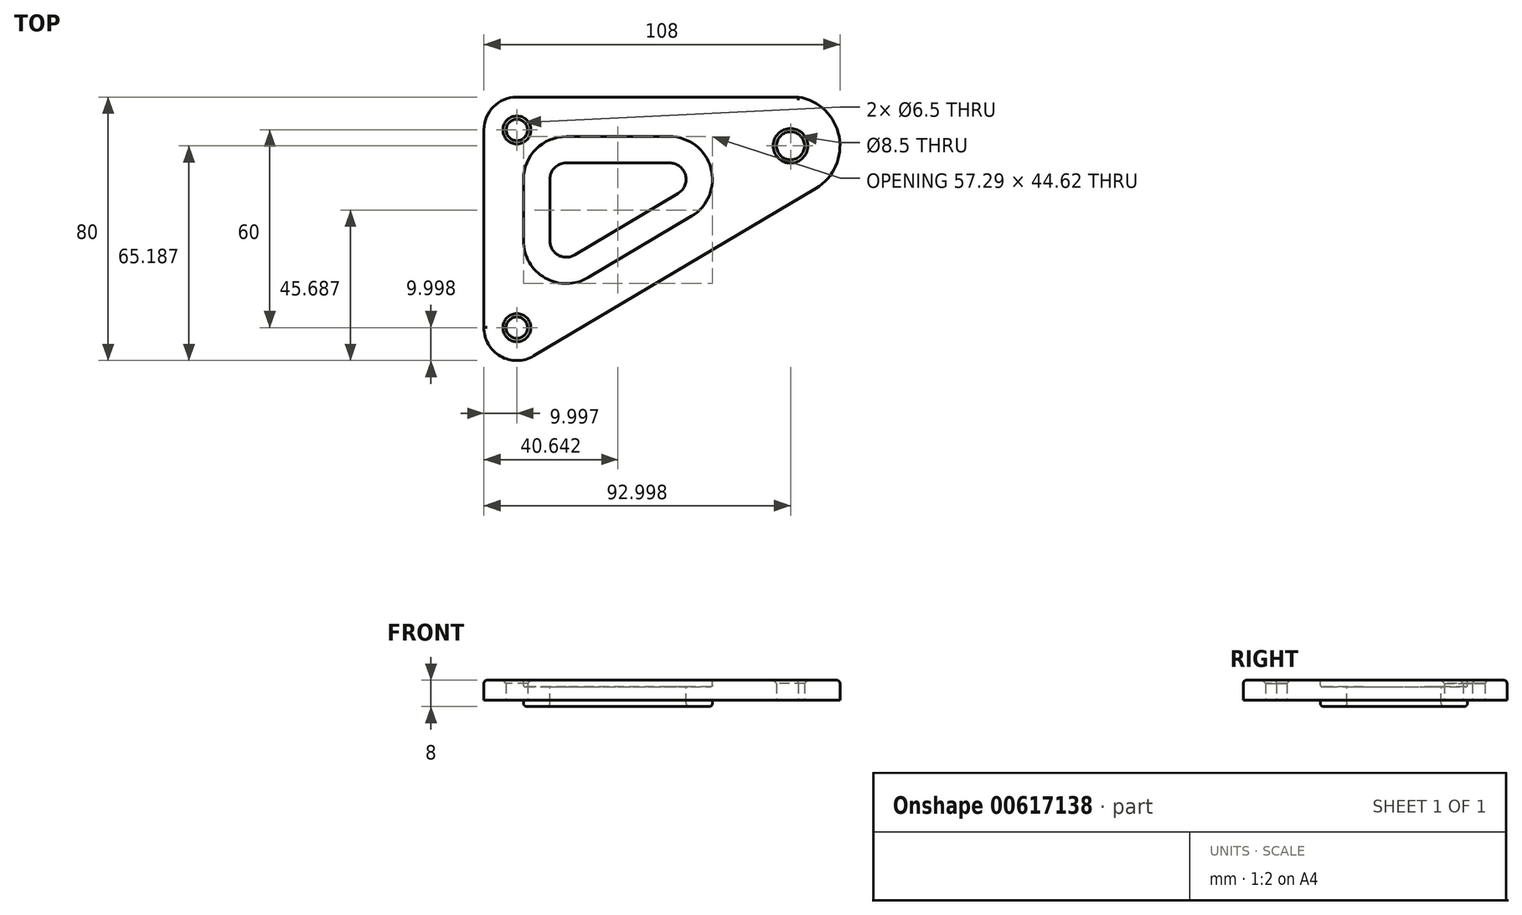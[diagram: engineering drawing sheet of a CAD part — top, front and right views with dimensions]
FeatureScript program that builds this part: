
annotation { "Feature Type Name" : "Feature", "Feature Type Description" : "" }
export const myFeature = defineFeature(function(context is Context, id is Id, definition is map)
    precondition{}
    {
        {
            var Q0;
            Q0=qCreatedBy(makeId("Top.planeOp"),FACE);
            var sketch = newSketch(context, id + "F0", { "sketchPlane" : qUnion([Q0])});
            skCircle(sketch, "E0", {"center": v(-62.86, 16.69) * mm, "radius": 3.25 * mm});
            skCircle(sketch, "E1", {"center": v(-62.86, -43.31) * mm, "radius": 3.25 * mm});
            skCircle(sketch, "E2", {"center": v(20.14, 11.88) * mm, "radius": 4.25 * mm});
            skArc(sketch, "E3", {"start": v(-62.86, 26.69) * mm, "mid": v(-69.93, 23.76) * mm, "end": v(-72.86, 16.69) * mm});
            skArc(sketch, "E4", {"start": v(-72.86, -43.2) * mm, "mid": v(-67.86, -51.98) * mm, "end": v(-57.75, -51.9) * mm});
            skArc(sketch, "E5", {"start": v(27.8, -1.01) * mm, "mid": v(34.24, 16.99) * mm, "end": v(17.76, 26.69) * mm});
            skLineSegment(sketch, "E6", {"start": v(-72.86, -43.2) * mm, "end": v(-72.86, 16.69) * mm});
            skLineSegment(sketch, "E7", {"start": v(-57.75, -51.9) * mm, "end": v(29.51, 0) * mm});
            skLineSegment(sketch, "E8", {"start": v(22.51, 26.69) * mm, "end": v(-62.86, 26.69) * mm});
            skSolve(sketch);
        }
        {
            var Q0;
            Q0=makeQuery(id+"F0.imprint","IMPRINT",FACE,{"disambiguationData":[TD([[makeQuery(id+"F0.imprint","IMPRINT",EDGE,{"derivedFrom":sQuery(id+"F0.wireOp",EDGE,"E0")}),-1.0]])]});
            extrude(context, id + "F1", {"entities" : qUnion([Q0]), "depth" : 8 * mm, "offsetDistance" : 25 * mm});
        }
        {
            var Q0;
            Q0=makeQuery(id+"F1.opExtrude","CAP_FACE",FACE,{"disambiguationData":[OSD([sQuery(id+"F0.wireOp",EDGE,"E0"),sQuery(id+"F0.wireOp",EDGE,"E1"),sQuery(id+"F0.wireOp",EDGE,"E2"),sQuery(id+"F0.wireOp",EDGE,"E3"),sQuery(id+"F0.wireOp",EDGE,"E4"),sQuery(id+"F0.wireOp",EDGE,"E5"),sQuery(id+"F0.wireOp",EDGE,"E6"),sQuery(id+"F0.wireOp",EDGE,"E7"),sQuery(id+"F0.wireOp",EDGE,"E8")])],"isStart":false});
            var sketch = newSketch(context, id + "F2", { "sketchPlane" : qUnion([Q0])});
            skLineSegment(sketch, "E9.0", {"start": v(-16.55, 6.69) * mm, "end": v(-47.86, 6.69) * mm});
            skLineSegment(sketch, "E9.1", {"start": v(-45.3, -21.23) * mm, "end": v(-14, -2.6) * mm});
            skLineSegment(sketch, "E9.2", {"start": v(-52.86, -16.94) * mm, "end": v(-52.86, 1.69) * mm});
            skPoint(sketch, "E10.visualSharp", {"position": v(-52.86, 6.69) * mm});
            skArc(sketch, "E10.filletArc", {"start": v(-47.86, 6.69) * mm, "mid": v(-51.4, 5.22) * mm, "end": v(-52.86, 1.69) * mm});
            skPoint(sketch, "E11.visualSharp", {"position": v(-52.86, -25.73) * mm});
            skArc(sketch, "E11.filletArc", {"start": v(-52.86, -16.94) * mm, "mid": v(-50.33, -21.28) * mm, "end": v(-45.3, -21.23) * mm});
            skPoint(sketch, "E12.visualSharp", {"position": v(1.63, 6.69) * mm});
            skArc(sketch, "E12.filletArc", {"start": v(-14, -2.6) * mm, "mid": v(-11.73, 3.01) * mm, "end": v(-16.55, 6.69) * mm});
            skSolve(sketch);
        }
        {
            var Q0;
            Q0=makeQuery(id+"F2.imprint","IMPRINT",FACE,{"disambiguationData":[TD([[makeQuery(id+"F2.imprint","IMPRINT",EDGE,{"derivedFrom":sQuery(id+"F2.wireOp",EDGE,"E9.0")}),1.0]])]});
            extrude(context, id + "F3", {"entities" : qUnion([Q0]), "operationType" : NewBodyOperationType.REMOVE, "oppositeDirection" : true, "depth" : 25 * mm, "offsetDistance" : 25 * mm});
        }
        {
            var Q0;
            Q0=makeQuery(id+"F1.opExtrude","CAP_FACE",FACE,{"disambiguationData":[OSD([sQuery(id+"F0.wireOp",EDGE,"E0"),sQuery(id+"F0.wireOp",EDGE,"E1"),sQuery(id+"F0.wireOp",EDGE,"E2"),sQuery(id+"F0.wireOp",EDGE,"E3"),sQuery(id+"F0.wireOp",EDGE,"E4"),sQuery(id+"F0.wireOp",EDGE,"E5"),sQuery(id+"F0.wireOp",EDGE,"E6"),sQuery(id+"F0.wireOp",EDGE,"E7"),sQuery(id+"F0.wireOp",EDGE,"E8")])],"isStart":false});
            var sketch = newSketch(context, id + "F4", { "sketchPlane" : qUnion([Q0])});
            skArc(sketch, "E13.0", {"start": v(-60.86, -16.94) * mm, "mid": v(-54.29, -28.24) * mm, "end": v(-41.22, -28.1) * mm});
            skArc(sketch, "E13.1", {"start": v(-47.86, 14.69) * mm, "mid": v(-57.05, 10.88) * mm, "end": v(-60.86, 1.69) * mm});
            skLineSegment(sketch, "E13.2", {"start": v(-16.55, 14.69) * mm, "end": v(-47.86, 14.69) * mm});
            skLineSegment(sketch, "E13.3", {"start": v(-60.86, -16.94) * mm, "end": v(-60.86, 1.69) * mm});
            skArc(sketch, "E13.4", {"start": v(-9.9, -9.48) * mm, "mid": v(-4.02, 5.13) * mm, "end": v(-16.55, 14.69) * mm});
            skLineSegment(sketch, "E13.5", {"start": v(-41.22, -28.1) * mm, "end": v(-9.9, -9.48) * mm});
            skArc(sketch, "E14.0", {"start": v(-77.86, -43.17) * mm, "mid": v(-70.34, -56.32) * mm, "end": v(-55.2, -56.2) * mm});
            skArc(sketch, "E14.1", {"start": v(30.36, -5.31) * mm, "mid": v(39.74, 15.84) * mm, "end": v(22.88, 31.69) * mm});
            skLineSegment(sketch, "E14.2", {"start": v(22.88, 31.69) * mm, "end": v(-62.86, 31.69) * mm});
            skLineSegment(sketch, "E14.3", {"start": v(-55.2, -56.2) * mm, "end": v(30.36, -5.31) * mm});
            skArc(sketch, "E14.4", {"start": v(-62.86, 31.69) * mm, "mid": v(-73.47, 27.3) * mm, "end": v(-77.86, 16.69) * mm});
            skLineSegment(sketch, "E14.5", {"start": v(-77.86, 16.69) * mm, "end": v(-77.86, -43.17) * mm});
            skSolve(sketch);
        }
        {
            var Q0;
            Q0=makeQuery(id+"F4.imprint","IMPRINT",FACE,{"disambiguationData":[TD([[makeQuery(id+"F4.imprint","IMPRINT",EDGE,{"derivedFrom":sQuery(id+"F4.wireOp",EDGE,"E13.0")}),1.0]])]});
            extrude(context, id + "F5", {"entities" : qUnion([Q0]), "operationType" : NewBodyOperationType.REMOVE, "oppositeDirection" : true, "depth" : 2 * mm, "offsetDistance" : 25 * mm});
        }
        {
            var Q0;
            Q0=makeQuery(id+"F1.opExtrude","CAP_FACE",FACE,{"disambiguationData":[OSD([sQuery(id+"F0.wireOp",EDGE,"E0"),sQuery(id+"F0.wireOp",EDGE,"E1"),sQuery(id+"F0.wireOp",EDGE,"E2"),sQuery(id+"F0.wireOp",EDGE,"E3"),sQuery(id+"F0.wireOp",EDGE,"E4"),sQuery(id+"F0.wireOp",EDGE,"E5"),sQuery(id+"F0.wireOp",EDGE,"E6"),sQuery(id+"F0.wireOp",EDGE,"E7"),sQuery(id+"F0.wireOp",EDGE,"E8")])],"isStart":true});
            var sketch = newSketch(context, id + "F6", { "sketchPlane" : qUnion([Q0])});
            skArc(sketch, "E15.0", {"start": v(-9.9, 9.48) * mm, "mid": v(-4.02, -5.13) * mm, "end": v(-16.55, -14.69) * mm});
            skArc(sketch, "E15.1", {"start": v(-47.86, -14.69) * mm, "mid": v(-57.05, -10.88) * mm, "end": v(-60.86, -1.69) * mm});
            skLineSegment(sketch, "E15.2", {"start": v(-60.86, 16.94) * mm, "end": v(-60.86, -1.69) * mm});
            skLineSegment(sketch, "E15.3", {"start": v(-16.55, -14.69) * mm, "end": v(-47.86, -14.69) * mm});
            skArc(sketch, "E15.4", {"start": v(-60.86, 16.94) * mm, "mid": v(-54.29, 28.24) * mm, "end": v(-41.22, 28.1) * mm});
            skLineSegment(sketch, "E15.5", {"start": v(-41.22, 28.1) * mm, "end": v(-9.9, 9.48) * mm});
            skSolve(sketch);
        }
        {
            var Q0;
            Q0=makeQuery(id+"F6.imprint","IMPRINT",FACE,{"disambiguationData":[TD([[makeQuery(id+"F6.imprint","IMPRINT",EDGE,{"derivedFrom":sQuery(id+"F6.wireOp",EDGE,"E15.0")}),-1.0]])]});
            extrude(context, id + "F7", {"entities" : qUnion([Q0]), "operationType" : NewBodyOperationType.REMOVE, "oppositeDirection" : true, "depth" : 2 * mm, "offsetDistance" : 25 * mm});
        }
        {
            var Q0;
            Q0=makeQuery(id+"F5.boolean.opBoolean","COPY",EDGE,{"derivedFrom":makeQuery(id+"F5.opExtrude","CAP_EDGE",EDGE,{"disambiguationData":[OSD([sQuery(id+"F4.wireOp",EDGE,"E13.1")])],"isStart":true})});
            var Q1;
            Q1=makeQuery(id+"F5.boolean.opBoolean","COPY",EDGE,{"derivedFrom":makeQuery(id+"F5.opExtrude","CAP_EDGE",EDGE,{"disambiguationData":[OSD([sQuery(id+"F4.wireOp",EDGE,"E13.2")])],"isStart":true})});
            var Q2;
            Q2=makeQuery(id+"F5.boolean.opBoolean","COPY",EDGE,{"derivedFrom":makeQuery(id+"F5.opExtrude","CAP_EDGE",EDGE,{"disambiguationData":[OSD([sQuery(id+"F4.wireOp",EDGE,"E13.4")])],"isStart":true})});
            var Q3;
            Q3=makeQuery(id+"F5.boolean.opBoolean","COPY",EDGE,{"derivedFrom":makeQuery(id+"F5.opExtrude","CAP_EDGE",EDGE,{"disambiguationData":[OSD([sQuery(id+"F4.wireOp",EDGE,"E13.5")])],"isStart":true})});
            var Q4;
            Q4=makeQuery(id+"F5.boolean.opBoolean","COPY",EDGE,{"derivedFrom":makeQuery(id+"F5.opExtrude","CAP_EDGE",EDGE,{"disambiguationData":[OSD([sQuery(id+"F4.wireOp",EDGE,"E13.0")])],"isStart":true})});
            var Q5;
            Q5=makeQuery(id+"F5.boolean.opBoolean","COPY",EDGE,{"derivedFrom":makeQuery(id+"F5.opExtrude","CAP_EDGE",EDGE,{"disambiguationData":[OSD([sQuery(id+"F4.wireOp",EDGE,"E13.3")])],"isStart":true})});
            var Q6;
            Q6=makeQuery(id+"F5.boolean.opBoolean","COPY",EDGE,{"derivedFrom":makeQuery(id+"F5.opExtrude","CAP_EDGE",EDGE,{"disambiguationData":[OSD([sQuery(id+"F2.wireOp",EDGE,"E9.2")])],"isStart":false})});
            var Q7;
            Q7=makeQuery(id+"F5.boolean.opBoolean","COPY",EDGE,{"derivedFrom":makeQuery(id+"F5.opExtrude","CAP_EDGE",EDGE,{"disambiguationData":[OSD([sQuery(id+"F2.wireOp",EDGE,"E10.filletArc")])],"isStart":false})});
            var Q8;
            Q8=makeQuery(id+"F5.boolean.opBoolean","COPY",EDGE,{"derivedFrom":makeQuery(id+"F5.opExtrude","CAP_EDGE",EDGE,{"disambiguationData":[OSD([sQuery(id+"F2.wireOp",EDGE,"E9.0")])],"isStart":false})});
            var Q9;
            Q9=makeQuery(id+"F5.boolean.opBoolean","COPY",FACE,{"derivedFrom":makeQuery(id+"F5.opExtrude","CAP_FACE",FACE,{"disambiguationData":[OSD([sQuery(id+"F2.wireOp",EDGE,"E9.0"),sQuery(id+"F2.wireOp",EDGE,"E9.1"),sQuery(id+"F2.wireOp",EDGE,"E9.2"),sQuery(id+"F2.wireOp",EDGE,"E10.filletArc"),sQuery(id+"F2.wireOp",EDGE,"E11.filletArc"),sQuery(id+"F2.wireOp",EDGE,"E12.filletArc"),sQuery(id+"F4.wireOp",EDGE,"E13.0"),sQuery(id+"F4.wireOp",EDGE,"E13.1"),sQuery(id+"F4.wireOp",EDGE,"E13.2"),sQuery(id+"F4.wireOp",EDGE,"E13.3"),sQuery(id+"F4.wireOp",EDGE,"E13.4"),sQuery(id+"F4.wireOp",EDGE,"E13.5")])],"isStart":false})});
            var Q10;
            Q10=makeQuery(id+"F7.boolean.opBoolean","COPY",EDGE,{"derivedFrom":makeQuery(id+"F7.opExtrude","CAP_EDGE",EDGE,{"disambiguationData":[OSD([sQuery(id+"F6.wireOp",EDGE,"E15.2")])],"isStart":true})});
            var Q11;
            Q11=makeQuery(id+"F7.boolean.opBoolean","COPY",EDGE,{"derivedFrom":makeQuery(id+"F7.opExtrude","CAP_EDGE",EDGE,{"disambiguationData":[OSD([sQuery(id+"F6.wireOp",EDGE,"E15.4")])],"isStart":true})});
            var Q12;
            Q12=makeQuery(id+"F7.boolean.opBoolean","COPY",EDGE,{"derivedFrom":makeQuery(id+"F7.opExtrude","CAP_EDGE",EDGE,{"disambiguationData":[OSD([sQuery(id+"F6.wireOp",EDGE,"E15.5")])],"isStart":true})});
            var Q13;
            Q13=makeQuery(id+"F7.boolean.opBoolean","COPY",EDGE,{"derivedFrom":makeQuery(id+"F7.opExtrude","CAP_EDGE",EDGE,{"disambiguationData":[OSD([sQuery(id+"F6.wireOp",EDGE,"E15.0")])],"isStart":true})});
            var Q14;
            Q14=makeQuery(id+"F7.boolean.opBoolean","COPY",EDGE,{"derivedFrom":makeQuery(id+"F7.opExtrude","CAP_EDGE",EDGE,{"disambiguationData":[OSD([sQuery(id+"F6.wireOp",EDGE,"E15.3")])],"isStart":true})});
            var Q15;
            Q15=makeQuery(id+"F7.boolean.opBoolean","COPY",EDGE,{"derivedFrom":makeQuery(id+"F7.opExtrude","CAP_EDGE",EDGE,{"disambiguationData":[OSD([sQuery(id+"F6.wireOp",EDGE,"E15.1")])],"isStart":true})});
            var Q16;
            Q16=makeQuery(id+"F7.boolean.opBoolean","COPY",EDGE,{"derivedFrom":makeQuery(id+"F7.opExtrude","CAP_EDGE",EDGE,{"disambiguationData":[OSD([sQuery(id+"F0.wireOp",EDGE,"E0"),sQuery(id+"F0.wireOp",EDGE,"E1"),sQuery(id+"F0.wireOp",EDGE,"E2"),sQuery(id+"F0.wireOp",EDGE,"E3"),sQuery(id+"F0.wireOp",EDGE,"E4"),sQuery(id+"F0.wireOp",EDGE,"E5"),sQuery(id+"F0.wireOp",EDGE,"E6"),sQuery(id+"F0.wireOp",EDGE,"E7"),sQuery(id+"F0.wireOp",EDGE,"E8"),sQuery(id+"F2.wireOp",EDGE,"E9.0")])],"isStart":false})});
            var Q17;
            Q17=makeQuery(id+"F7.boolean.opBoolean","COPY",EDGE,{"derivedFrom":makeQuery(id+"F7.opExtrude","CAP_EDGE",EDGE,{"disambiguationData":[OSD([sQuery(id+"F0.wireOp",EDGE,"E0"),sQuery(id+"F0.wireOp",EDGE,"E1"),sQuery(id+"F0.wireOp",EDGE,"E2"),sQuery(id+"F0.wireOp",EDGE,"E3"),sQuery(id+"F0.wireOp",EDGE,"E4"),sQuery(id+"F0.wireOp",EDGE,"E5"),sQuery(id+"F0.wireOp",EDGE,"E6"),sQuery(id+"F0.wireOp",EDGE,"E7"),sQuery(id+"F0.wireOp",EDGE,"E8"),sQuery(id+"F2.wireOp",EDGE,"E10.filletArc")])],"isStart":false})});
            var Q18;
            Q18=makeQuery(id+"F7.boolean.opBoolean","COPY",EDGE,{"derivedFrom":makeQuery(id+"F7.opExtrude","CAP_EDGE",EDGE,{"disambiguationData":[OSD([sQuery(id+"F0.wireOp",EDGE,"E0"),sQuery(id+"F0.wireOp",EDGE,"E1"),sQuery(id+"F0.wireOp",EDGE,"E2"),sQuery(id+"F0.wireOp",EDGE,"E3"),sQuery(id+"F0.wireOp",EDGE,"E4"),sQuery(id+"F0.wireOp",EDGE,"E5"),sQuery(id+"F0.wireOp",EDGE,"E6"),sQuery(id+"F0.wireOp",EDGE,"E7"),sQuery(id+"F0.wireOp",EDGE,"E8"),sQuery(id+"F2.wireOp",EDGE,"E9.2")])],"isStart":false})});
            var Q19;
            Q19=makeQuery(id+"F7.boolean.opBoolean","COPY",EDGE,{"derivedFrom":makeQuery(id+"F7.opExtrude","CAP_EDGE",EDGE,{"disambiguationData":[OSD([sQuery(id+"F0.wireOp",EDGE,"E0"),sQuery(id+"F0.wireOp",EDGE,"E1"),sQuery(id+"F0.wireOp",EDGE,"E2"),sQuery(id+"F0.wireOp",EDGE,"E3"),sQuery(id+"F0.wireOp",EDGE,"E4"),sQuery(id+"F0.wireOp",EDGE,"E5"),sQuery(id+"F0.wireOp",EDGE,"E6"),sQuery(id+"F0.wireOp",EDGE,"E7"),sQuery(id+"F0.wireOp",EDGE,"E8"),sQuery(id+"F2.wireOp",EDGE,"E11.filletArc")])],"isStart":false})});
            var Q20;
            Q20=makeQuery(id+"F7.boolean.opBoolean","COPY",EDGE,{"derivedFrom":makeQuery(id+"F7.opExtrude","CAP_EDGE",EDGE,{"disambiguationData":[OSD([sQuery(id+"F0.wireOp",EDGE,"E0"),sQuery(id+"F0.wireOp",EDGE,"E1"),sQuery(id+"F0.wireOp",EDGE,"E2"),sQuery(id+"F0.wireOp",EDGE,"E3"),sQuery(id+"F0.wireOp",EDGE,"E4"),sQuery(id+"F0.wireOp",EDGE,"E5"),sQuery(id+"F0.wireOp",EDGE,"E6"),sQuery(id+"F0.wireOp",EDGE,"E7"),sQuery(id+"F0.wireOp",EDGE,"E8"),sQuery(id+"F2.wireOp",EDGE,"E9.1")])],"isStart":false})});
            var Q21;
            Q21=makeQuery(id+"F7.boolean.opBoolean","COPY",EDGE,{"derivedFrom":makeQuery(id+"F7.opExtrude","CAP_EDGE",EDGE,{"disambiguationData":[OSD([sQuery(id+"F0.wireOp",EDGE,"E0"),sQuery(id+"F0.wireOp",EDGE,"E1"),sQuery(id+"F0.wireOp",EDGE,"E2"),sQuery(id+"F0.wireOp",EDGE,"E3"),sQuery(id+"F0.wireOp",EDGE,"E4"),sQuery(id+"F0.wireOp",EDGE,"E5"),sQuery(id+"F0.wireOp",EDGE,"E6"),sQuery(id+"F0.wireOp",EDGE,"E7"),sQuery(id+"F0.wireOp",EDGE,"E8"),sQuery(id+"F2.wireOp",EDGE,"E12.filletArc")])],"isStart":false})});
            fillet(context, id + "F8", {"entities" : qUnion([Q0, Q1, Q2, Q3, Q4, Q5, Q6, Q7, Q8, Q9, Q10, Q11, Q12, Q13, Q14, Q15, Q16, Q17, Q18, Q19, Q20, Q21]), "radius" : 0.5 * mm, "tangentPropagation" : true, "allowEdgeOverflow" : false});
        }
        {
            var Q0;
            Q0=makeQuery(id+"F1.opExtrude","CAP_EDGE",EDGE,{"disambiguationData":[OSD([sQuery(id+"F0.wireOp",EDGE,"E3")])],"isStart":true});
            var Q1;
            Q1=makeQuery(id+"F1.opExtrude","CAP_EDGE",EDGE,{"disambiguationData":[OSD([sQuery(id+"F0.wireOp",EDGE,"E6")])],"isStart":true});
            var Q2;
            Q2=makeQuery(id+"F1.opExtrude","CAP_EDGE",EDGE,{"disambiguationData":[OSD([sQuery(id+"F0.wireOp",EDGE,"E4")])],"isStart":true});
            var Q3;
            Q3=makeQuery(id+"F1.opExtrude","CAP_EDGE",EDGE,{"disambiguationData":[OSD([sQuery(id+"F0.wireOp",EDGE,"E7")])],"isStart":true});
            var Q4;
            Q4=makeQuery(id+"F1.opExtrude","CAP_EDGE",EDGE,{"disambiguationData":[OSD([sQuery(id+"F0.wireOp",EDGE,"E5")])],"isStart":true});
            var Q5;
            Q5=makeQuery(id+"F1.opExtrude","CAP_FACE",FACE,{"disambiguationData":[OSD([sQuery(id+"F0.wireOp",EDGE,"E0"),sQuery(id+"F0.wireOp",EDGE,"E1"),sQuery(id+"F0.wireOp",EDGE,"E2"),sQuery(id+"F0.wireOp",EDGE,"E3"),sQuery(id+"F0.wireOp",EDGE,"E4"),sQuery(id+"F0.wireOp",EDGE,"E5"),sQuery(id+"F0.wireOp",EDGE,"E6"),sQuery(id+"F0.wireOp",EDGE,"E7"),sQuery(id+"F0.wireOp",EDGE,"E8")])],"isStart":true});
            var Q6;
            Q6=makeQuery(id+"F1.opExtrude","CAP_EDGE",EDGE,{"disambiguationData":[OSD([sQuery(id+"F0.wireOp",EDGE,"E5")])],"isStart":false});
            var Q7;
            Q7=makeQuery(id+"F1.opExtrude","CAP_EDGE",EDGE,{"disambiguationData":[OSD([sQuery(id+"F0.wireOp",EDGE,"E7")])],"isStart":false});
            var Q8;
            Q8=makeQuery(id+"F1.opExtrude","CAP_EDGE",EDGE,{"disambiguationData":[OSD([sQuery(id+"F0.wireOp",EDGE,"E4")])],"isStart":false});
            var Q9;
            Q9=makeQuery(id+"F1.opExtrude","CAP_EDGE",EDGE,{"disambiguationData":[OSD([sQuery(id+"F0.wireOp",EDGE,"E6")])],"isStart":false});
            var Q10;
            Q10=makeQuery(id+"F1.opExtrude","CAP_EDGE",EDGE,{"disambiguationData":[OSD([sQuery(id+"F0.wireOp",EDGE,"E3")])],"isStart":false});
            var Q11;
            Q11=makeQuery(id+"F1.opExtrude","CAP_EDGE",EDGE,{"disambiguationData":[OSD([sQuery(id+"F0.wireOp",EDGE,"E8")])],"isStart":false});
            fillet(context, id + "F9", {"entities" : qUnion([Q0, Q1, Q2, Q3, Q4, Q5, Q6, Q7, Q8, Q9, Q10, Q11]), "radius" : 1 * mm, "tangentPropagation" : true, "allowEdgeOverflow" : false});
        }
        {
            var Q0;
            Q0=makeQuery(id+"F1.opExtrude","CAP_EDGE",EDGE,{"disambiguationData":[OSD([sQuery(id+"F0.wireOp",EDGE,"E2")])],"isStart":false});
            var Q1;
            Q1=makeQuery(id+"F1.opExtrude","CAP_EDGE",EDGE,{"disambiguationData":[OSD([sQuery(id+"F0.wireOp",EDGE,"E1")])],"isStart":false});
            var Q2;
            Q2=makeQuery(id+"F1.opExtrude","CAP_EDGE",EDGE,{"disambiguationData":[OSD([sQuery(id+"F0.wireOp",EDGE,"E0")])],"isStart":false});
            chamfer(context, id + "F10", {"entities" : qUnion([Q0, Q1, Q2]), "width" : 1 * mm, "tangentPropagation" : true});
        }
    });
